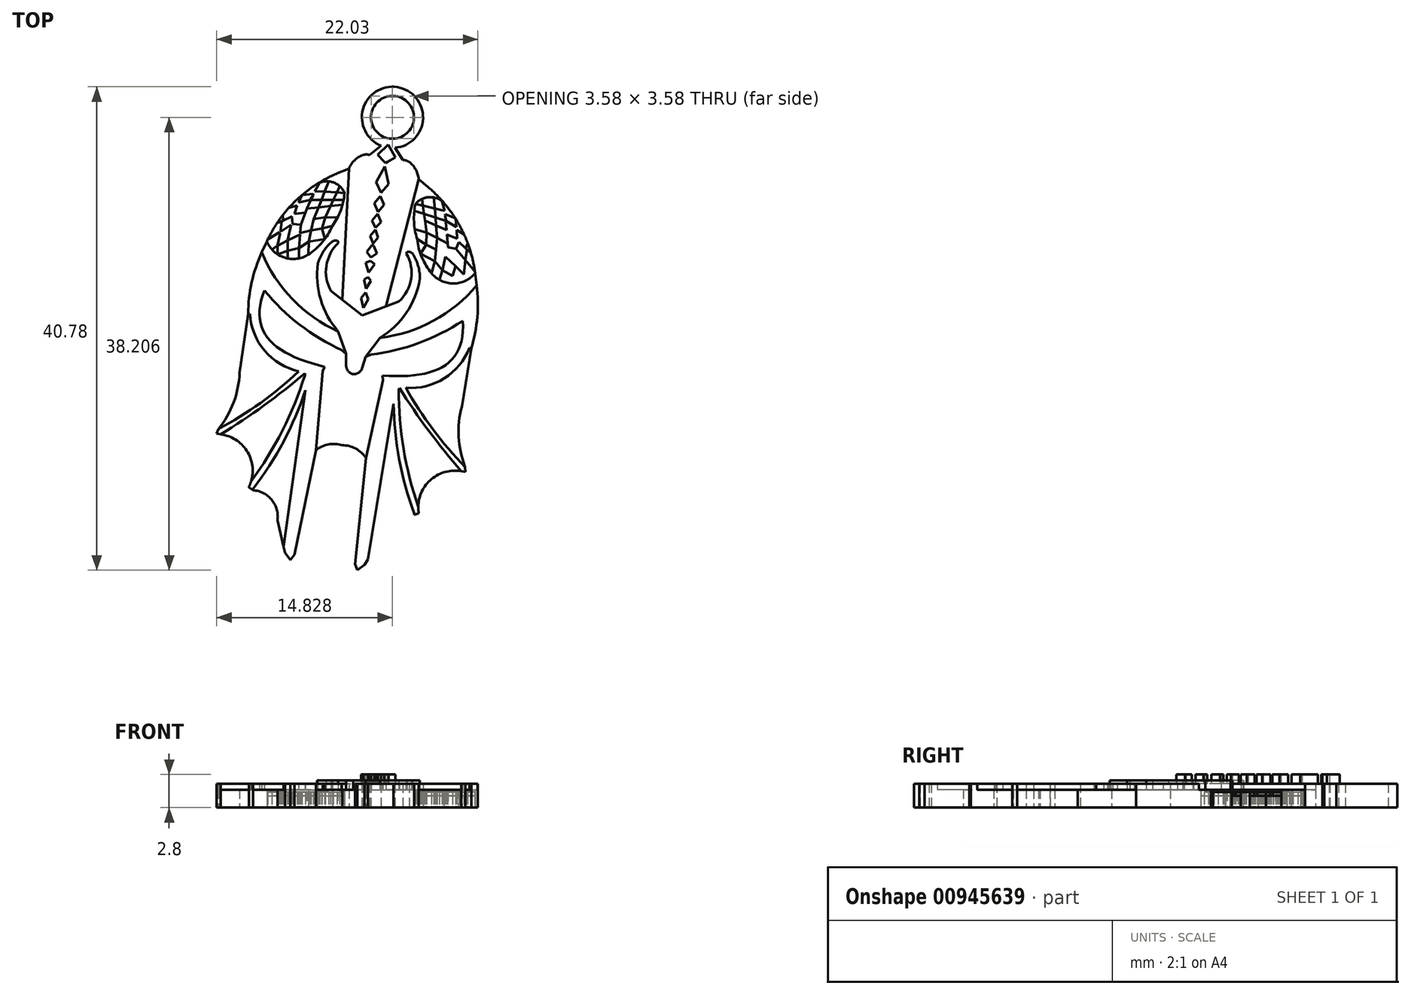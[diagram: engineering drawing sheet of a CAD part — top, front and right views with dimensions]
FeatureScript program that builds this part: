
annotation { "Feature Type Name" : "Feature", "Feature Type Description" : "" }
export const myFeature = defineFeature(function(context is Context, id is Id, definition is map)
    precondition{}
    {
        {
            var Q0;
            Q0=qCreatedBy(makeId("Top.planeOp"),FACE);
            var sketch = newSketch(context, id + "F0", { "sketchPlane" : qUnion([Q0])});
            skLineSegment(sketch, "E0", {"start": v(-25.56, -12.14) * mm, "end": v(-27.36, -20.95) * mm});
            skLineSegment(sketch, "E1", {"start": v(-25.56, -12.14) * mm, "end": v(-24.96, -5.46) * mm});
            skLineSegment(sketch, "E2", {"start": v(-24.96, -5.46) * mm, "end": v(-24.8, -5.09) * mm});
            skFitSpline(sketch, "E3", {"points": [v(-24.8, -5.09) * mm, v(-29.9, 1.35) * mm], "startDerivative": vector(-13.26, 3.2) * mm, "endDerivative": vector(4.1, 10.34) * mm});
            skLineSegment(sketch, "E4", {"start": v(-27.36, -20.95) * mm, "end": v(-27.7, -21.38) * mm});
            skLineSegment(sketch, "E5", {"start": v(-21.36, -21.48) * mm, "end": v(-21.23, -22.05) * mm});
            skArc(sketch, "E6", {"start": v(-29.9, 1.35) * mm, "mid": v(-26.93, -1.53) * mm, "end": v(-23.38, -3.66) * mm});
            skLineSegment(sketch, "E7", {"start": v(-19.37, 14.19) * mm, "end": v(-25.29, -24.47) * mm});
            skArc(sketch, "E8", {"start": v(-31.21, -15.24) * mm, "mid": v(-31.25, -12.4) * mm, "end": v(-33.58, -10.79) * mm});
            skArc(sketch, "E9", {"start": v(-28.8, -18.07) * mm, "mid": v(-29.26, -16.34) * mm, "end": v(-30.84, -15.5) * mm});
            skLineSegment(sketch, "E10", {"start": v(-28.8, -18.07) * mm, "end": v(-28.16, -20.77) * mm});
            skLineSegment(sketch, "E11", {"start": v(-28.16, -20.77) * mm, "end": v(-27.7, -21.38) * mm});
            skLineSegment(sketch, "E12", {"start": v(-31.21, -15.24) * mm, "end": v(-30.84, -15.5) * mm});
            skArc(sketch, "E13", {"start": v(-33.78, -10.35) * mm, "mid": v(-32.5, -8.1) * mm, "end": v(-31.98, -5.57) * mm});
            skLineSegment(sketch, "E14", {"start": v(-33.78, -10.35) * mm, "end": v(-33.92, -10.73) * mm});
            skLineSegment(sketch, "E15", {"start": v(-33.92, -10.73) * mm, "end": v(-33.58, -10.79) * mm});
            skLineSegment(sketch, "E16", {"start": v(-31.98, -5.57) * mm, "end": v(-31.26, -0.63) * mm});
            skArc(sketch, "E17", {"start": v(-30.12, 4.57) * mm, "mid": v(-30.97, 2.04) * mm, "end": v(-31.26, -0.63) * mm});
            skLineSegment(sketch, "E18", {"start": v(-30.12, 4.57) * mm, "end": v(-29.69, 5.5) * mm});
            skArc(sketch, "E19", {"start": v(-23.73, 11.24) * mm, "mid": v(-27.25, 8.93) * mm, "end": v(-29.69, 5.5) * mm});
            skLineSegment(sketch, "E20", {"start": v(-23.73, 11.24) * mm, "end": v(-22.77, 11.65) * mm});
            skArc(sketch, "E21", {"start": v(-21.57, 12.8) * mm, "mid": v(-22.29, 12.34) * mm, "end": v(-22.77, 11.65) * mm});
            skArc(sketch, "E22", {"start": v(-21.01, 12.8) * mm, "mid": v(-21.3, 12.83) * mm, "end": v(-21.57, 12.8) * mm});
            skLineSegment(sketch, "E23", {"start": v(-21.01, 12.8) * mm, "end": v(-19.98, 13.65) * mm});
            skLineSegment(sketch, "E24", {"start": v(-19.98, 13.65) * mm, "end": v(-19.37, 14.18) * mm});
            skArc(sketch, "E25", {"start": v(-23.34, -11.72) * mm, "mid": v(-24.5, -11.64) * mm, "end": v(-25.56, -12.14) * mm});
            skLineSegment(sketch, "E26", {"start": v(-23.38, -3.66) * mm, "end": v(-23, -4) * mm});
            skLineSegment(sketch, "E27", {"start": v(-23, -4) * mm, "end": v(-23, -4.97) * mm});
            skArc(sketch, "E28", {"start": v(-23, -4.97) * mm, "mid": v(-22.83, -5.44) * mm, "end": v(-22.42, -5.71) * mm});
            skArc(sketch, "E29", {"start": v(-31.12, -0.63) * mm, "mid": v(-29.87, -3.73) * mm, "end": v(-27, -5.47) * mm});
            skLineSegment(sketch, "E30", {"start": v(-31.12, -0.63) * mm, "end": v(-31.26, -0.63) * mm});
            skArc(sketch, "E31", {"start": v(-33.78, -10.35) * mm, "mid": v(-30.23, -8.13) * mm, "end": v(-27, -5.47) * mm});
            skArc(sketch, "E32", {"start": v(-33.58, -10.79) * mm, "mid": v(-29.93, -8.35) * mm, "end": v(-26.48, -5.64) * mm});
            skArc(sketch, "E33", {"start": v(-31.02, -14.75) * mm, "mid": v(-28.38, -10.47) * mm, "end": v(-26.48, -5.8) * mm});
            skLineSegment(sketch, "E34", {"start": v(-26.48, -5.8) * mm, "end": v(-26.48, -5.64) * mm});
            skArc(sketch, "E35", {"start": v(-30.84, -15.38) * mm, "mid": v(-28.29, -11.4) * mm, "end": v(-26.42, -7.06) * mm});
            skPoint(sketch, "E35.startSnap0", {"position": v(-31.03, -15.38) * mm});
            skLineSegment(sketch, "E36", {"start": v(-26.42, -7.06) * mm, "end": v(-28.28, -20.26) * mm});
            skArc(sketch, "E37", {"start": v(-30.12, 4.57) * mm, "mid": v(-27.53, 0.62) * mm, "end": v(-23.66, -2.1) * mm});
            skLineSegment(sketch, "E38", {"start": v(-23.66, -2.1) * mm, "end": v(-23, -4) * mm});
            skArc(sketch, "E39", {"start": v(-29.69, 5.5) * mm, "mid": v(-28.2, 4.12) * mm, "end": v(-26.19, 4.39) * mm});
            skArc(sketch, "E40", {"start": v(-26.19, 4.39) * mm, "mid": v(-25, 5.44) * mm, "end": v(-24.15, 6.8) * mm});
            skArc(sketch, "E41", {"start": v(-24.15, 6.8) * mm, "mid": v(-23.46, 8.12) * mm, "end": v(-23.14, 9.58) * mm});
            skArc(sketch, "E42", {"start": v(-23.14, 9.58) * mm, "mid": v(-24.22, 10.52) * mm, "end": v(-25.62, 10.24) * mm});
            skArc(sketch, "E43", {"start": v(-25.39, 3.66) * mm, "mid": v(-25.15, 0.59) * mm, "end": v(-23.66, -2.1) * mm});
            skArc(sketch, "E44", {"start": v(-24.15, 5.5) * mm, "mid": v(-24.9, 4.67) * mm, "end": v(-25.39, 3.66) * mm});
            skArc(sketch, "E45", {"start": v(-23.66, 5.5) * mm, "mid": v(-23.9, 5.57) * mm, "end": v(-24.15, 5.5) * mm});
            skLineSegment(sketch, "E46", {"start": v(-23.66, 5.5) * mm, "end": v(-23.66, 5.35) * mm});
            skArc(sketch, "E47", {"start": v(-23.66, 5.35) * mm, "mid": v(-24.67, 3.43) * mm, "end": v(-24.26, 1.3) * mm});
            skLineSegment(sketch, "E48", {"start": v(-24.26, 1.3) * mm, "end": v(-21.66, -0.76) * mm});
            skLineSegment(sketch, "E49", {"start": v(-22.77, 11.65) * mm, "end": v(-23.33, 0.57) * mm});
            skLineSegment(sketch, "E50", {"start": v(-29.62, 5.65) * mm, "end": v(-28.62, 6.27) * mm});
            skLineSegment(sketch, "E51", {"start": v(-28.54, 6.4) * mm, "end": v(-28.42, 7.15) * mm});
            skLineSegment(sketch, "E52", {"start": v(-28.42, 7.15) * mm, "end": v(-28.82, 7.06) * mm});
            skLineSegment(sketch, "E53", {"start": v(-28.82, 7.06) * mm, "end": v(-28.3, 7.26) * mm});
            skLineSegment(sketch, "E54", {"start": v(-28.3, 7.26) * mm, "end": v(-28.34, 7.72) * mm});
            skLineSegment(sketch, "E55", {"start": v(-28.3, 7.26) * mm, "end": v(-28.42, 7.15) * mm});
            skLineSegment(sketch, "E56", {"start": v(-27.6, 7.6) * mm, "end": v(-28.3, 7.26) * mm});
            skLineSegment(sketch, "E57", {"start": v(-27.6, 7.6) * mm, "end": v(-27.53, 6.98) * mm});
            skLineSegment(sketch, "E58", {"start": v(-27.53, 6.98) * mm, "end": v(-28.5, 6.34) * mm});
            skLineSegment(sketch, "E59", {"start": v(-27.82, 8.34) * mm, "end": v(-27.12, 8.53) * mm});
            skLineSegment(sketch, "E60", {"start": v(-27.12, 8.53) * mm, "end": v(-27.35, 7.83) * mm});
            skLineSegment(sketch, "E61", {"start": v(-27.35, 7.83) * mm, "end": v(-27.6, 7.6) * mm});
            skLineSegment(sketch, "E62", {"start": v(-27.12, 8.53) * mm, "end": v(-26.72, 9.42) * mm});
            skLineSegment(sketch, "E63", {"start": v(-26.72, 9.42) * mm, "end": v(-25.79, 9.51) * mm});
            skLineSegment(sketch, "E64", {"start": v(-25.79, 9.51) * mm, "end": v(-25.22, 10.46) * mm});
            skLineSegment(sketch, "E65", {"start": v(-25.79, 9.4) * mm, "end": v(-26.04, 8.99) * mm});
            skLineSegment(sketch, "E66", {"start": v(-26.04, 8.99) * mm, "end": v(-27.02, 8.76) * mm});
            skLineSegment(sketch, "E67", {"start": v(-26.04, 8.9) * mm, "end": v(-26.84, 6.92) * mm});
            skLineSegment(sketch, "E68", {"start": v(-26.84, 6.92) * mm, "end": v(-27.53, 6.98) * mm});
            skLineSegment(sketch, "E69", {"start": v(-26.44, 7.9) * mm, "end": v(-27.35, 7.83) * mm});
            skLineSegment(sketch, "E70", {"start": v(-25.79, 9.4) * mm, "end": v(-25.79, 9.51) * mm});
            skLineSegment(sketch, "E71", {"start": v(-26.04, 8.9) * mm, "end": v(-26.04, 8.99) * mm});
            skLineSegment(sketch, "E72", {"start": v(-28.58, 6.2) * mm, "end": v(-28.78, 5.16) * mm});
            skLineSegment(sketch, "E73", {"start": v(-28.81, 5.11) * mm, "end": v(-29.26, 4.82) * mm});
            skLineSegment(sketch, "E74", {"start": v(-28.8, 5.1) * mm, "end": v(-28.8, 4.4) * mm});
            skLineSegment(sketch, "E75", {"start": v(-28.8, 4.4) * mm, "end": v(-27.93, 4.72) * mm});
            skLineSegment(sketch, "E76", {"start": v(-27.93, 4.72) * mm, "end": v(-27.93, 5.53) * mm});
            skLineSegment(sketch, "E77", {"start": v(-27.98, 5.57) * mm, "end": v(-28.78, 5.13) * mm});
            skLineSegment(sketch, "E78", {"start": v(-27.92, 5.64) * mm, "end": v(-27.64, 6.9) * mm});
            skLineSegment(sketch, "E79", {"start": v(-27.64, 6.9) * mm, "end": v(-27.92, 5.64) * mm});
            skLineSegment(sketch, "E80", {"start": v(-27.9, 5.6) * mm, "end": v(-26.88, 6.07) * mm});
            skLineSegment(sketch, "E81", {"start": v(-26.88, 6.07) * mm, "end": v(-26.84, 6.92) * mm});
            skLineSegment(sketch, "E82", {"start": v(-26.88, 6.07) * mm, "end": v(-26.98, 4.92) * mm});
            skLineSegment(sketch, "E83", {"start": v(-26.98, 4.92) * mm, "end": v(-27.93, 4.72) * mm});
            skLineSegment(sketch, "E84", {"start": v(-26.98, 4.92) * mm, "end": v(-26.98, 4.06) * mm});
            skLineSegment(sketch, "E85", {"start": v(-26.98, 4.06) * mm, "end": v(-26.98, 4.92) * mm});
            skLineSegment(sketch, "E86", {"start": v(-26.98, 4.92) * mm, "end": v(-26.15, 5.47) * mm});
            skLineSegment(sketch, "E87", {"start": v(-26.15, 5.47) * mm, "end": v(-26.19, 4.39) * mm});
            skLineSegment(sketch, "E88", {"start": v(-26.15, 5.47) * mm, "end": v(-24.8, 5.7) * mm});
            skLineSegment(sketch, "E89", {"start": v(-24.8, 5.7) * mm, "end": v(-25.04, 6.57) * mm});
            skLineSegment(sketch, "E90", {"start": v(-25.04, 6.57) * mm, "end": v(-25.95, 6.41) * mm});
            skLineSegment(sketch, "E91", {"start": v(-25.95, 6.41) * mm, "end": v(-26.88, 6.2) * mm});
            skLineSegment(sketch, "E92", {"start": v(-26.88, 6.2) * mm, "end": v(-25.95, 6.41) * mm});
            skLineSegment(sketch, "E93", {"start": v(-25.95, 6.41) * mm, "end": v(-26.15, 5.47) * mm});
            skLineSegment(sketch, "E94", {"start": v(-25.04, 6.57) * mm, "end": v(-24.15, 6.8) * mm});
            skLineSegment(sketch, "E95", {"start": v(-25.04, 6.57) * mm, "end": v(-24.75, 7.55) * mm});
            skLineSegment(sketch, "E96", {"start": v(-24.75, 7.55) * mm, "end": v(-23.72, 7.51) * mm});
            skLineSegment(sketch, "E97", {"start": v(-23.72, 7.51) * mm, "end": v(-24.75, 7.55) * mm});
            skLineSegment(sketch, "E98", {"start": v(-24.75, 7.55) * mm, "end": v(-26.72, 7.2) * mm});
            skLineSegment(sketch, "E99", {"start": v(-26.72, 7.2) * mm, "end": v(-25.74, 7.38) * mm});
            skLineSegment(sketch, "E100", {"start": v(-25.74, 7.38) * mm, "end": v(-25.95, 6.41) * mm});
            skLineSegment(sketch, "E101", {"start": v(-25.74, 7.38) * mm, "end": v(-24.45, 10.56) * mm});
            skLineSegment(sketch, "E102", {"start": v(-24.75, 7.55) * mm, "end": v(-23.53, 10.14) * mm});
            skLineSegment(sketch, "E103", {"start": v(-26.3, 8.25) * mm, "end": v(-23.3, 8.6) * mm});
            skLineSegment(sketch, "E104", {"start": v(-25.65, 9.74) * mm, "end": v(-23.14, 9.58) * mm});
            skLineSegment(sketch, "E105", {"start": v(-26.04, 8.99) * mm, "end": v(-23.22, 8.99) * mm});
            skLineSegment(sketch, "E106", {"start": v(-20.95, 3.86) * mm, "end": v(-21.37, 3.69) * mm});
            skLineSegment(sketch, "E107", {"start": v(-21.37, 3.69) * mm, "end": v(-21.1, 2.86) * mm});
            skLineSegment(sketch, "E108", {"start": v(-21.16, 2.5) * mm, "end": v(-21.5, 2.27) * mm});
            skLineSegment(sketch, "E109", {"start": v(-21.5, 2.27) * mm, "end": v(-21.3, 1.5) * mm});
            skLineSegment(sketch, "E110", {"start": v(-21.36, 1.2) * mm, "end": v(-21.74, 0.71) * mm});
            skLineSegment(sketch, "E111", {"start": v(-21.74, 0.71) * mm, "end": v(-21.56, -0.12) * mm});
            skLineSegment(sketch, "E112", {"start": v(-19.45, 13.66) * mm, "end": v(-20.34, 12.81) * mm});
            skLineSegment(sketch, "E113", {"start": v(-20.34, 12.81) * mm, "end": v(-19.8, 12.25) * mm});
            skLineSegment(sketch, "E114", {"start": v(-19.73, 11.84) * mm, "end": v(-20.48, 10.49) * mm});
            skLineSegment(sketch, "E115", {"start": v(-20.48, 10.49) * mm, "end": v(-20.07, 9.6) * mm});
            skLineSegment(sketch, "E116", {"start": v(-19.8, 12.25) * mm, "end": v(-19.68, 12.12) * mm});
            skLineSegment(sketch, "E117", {"start": v(-20.8, 5.17) * mm, "end": v(-21.27, 4.62) * mm});
            skLineSegment(sketch, "E118", {"start": v(-21.27, 4.62) * mm, "end": v(-20.9, 4.14) * mm});
            skLineSegment(sketch, "E119", {"start": v(-20.55, 6.5) * mm, "end": v(-20.98, 5.94) * mm});
            skLineSegment(sketch, "E120", {"start": v(-20.98, 5.94) * mm, "end": v(-20.72, 5.32) * mm});
            skLineSegment(sketch, "E121", {"start": v(-20.34, 7.83) * mm, "end": v(-20.82, 7.24) * mm});
            skLineSegment(sketch, "E122", {"start": v(-20.82, 7.24) * mm, "end": v(-20.52, 6.65) * mm});
            skLineSegment(sketch, "E123", {"start": v(-20.11, 9.32) * mm, "end": v(-20.64, 8.7) * mm});
            skLineSegment(sketch, "E124", {"start": v(-20.64, 8.7) * mm, "end": v(-20.32, 8) * mm});
            skLineSegment(sketch, "E125.MirrorCS", {"start": v(-13.49, 5.43) * mm, "end": v(-12.92, 4.9) * mm});
            skLineSegment(sketch, "E126.MirrorCS", {"start": v(-13.77, 3.42) * mm, "end": v(-13.65, 4.76) * mm});
            skLineSegment(sketch, "E127.MirrorCS", {"start": v(-12.92, 4.9) * mm, "end": v(-12.74, 5.33) * mm});
            skLineSegment(sketch, "E128.MirrorCS", {"start": v(-14.6, 4.32) * mm, "end": v(-15.4, 4.8) * mm});
            skLineSegment(sketch, "E129.MirrorCS", {"start": v(-14.59, 7.14) * mm, "end": v(-14.56, 7.23) * mm});
            skLineSegment(sketch, "E130.MirrorCS", {"start": v(-14.67, 7.7) * mm, "end": v(-14.64, 7.8) * mm});
            skLineSegment(sketch, "E131.MirrorCS", {"start": v(-12.48, 4.56) * mm, "end": v(-12.92, 4.9) * mm});
            skLineSegment(sketch, "E132.MirrorCS", {"start": v(-13.65, 4.76) * mm, "end": v(-13.77, 3.42) * mm});
            skLineSegment(sketch, "E133.MirrorCS", {"start": v(-13.49, 5.43) * mm, "end": v(-13.73, 4.87) * mm});
            skLineSegment(sketch, "E134.MirrorCS", {"start": v(-14.63, 4.19) * mm, "end": v(-14.42, 5.01) * mm});
            skLineSegment(sketch, "E135.MirrorCS", {"start": v(-13.66, 6.47) * mm, "end": v(-13.65, 5.73) * mm});
            skLineSegment(sketch, "E136.MirrorCS", {"start": v(-15.4, 4.8) * mm, "end": v(-14.6, 4.32) * mm});
            skLineSegment(sketch, "E137.MirrorCS", {"start": v(-14.44, 5.32) * mm, "end": v(-15.33, 5.78) * mm});
            skLineSegment(sketch, "E138.MirrorCS", {"start": v(-13.66, 6.47) * mm, "end": v(-13.78, 7.43) * mm});
            skLineSegment(sketch, "E139.MirrorCS", {"start": v(-13.73, 4.87) * mm, "end": v(-12.95, 3.91) * mm});
            skLineSegment(sketch, "E140.MirrorCS", {"start": v(-14.5, 6.08) * mm, "end": v(-13.65, 5.73) * mm});
            skLineSegment(sketch, "E141.MirrorCS", {"start": v(-12.14, 2.97) * mm, "end": v(-12.95, 3.91) * mm});
            skLineSegment(sketch, "E142.MirrorCS", {"start": v(-14.56, 7.23) * mm, "end": v(-13.69, 6.72) * mm});
            skLineSegment(sketch, "E143.MirrorCS", {"start": v(-13.05, 6.08) * mm, "end": v(-13.66, 6.47) * mm});
            skLineSegment(sketch, "E144.MirrorCS", {"start": v(-14.67, 7.7) * mm, "end": v(-14.56, 7.23) * mm});
            skLineSegment(sketch, "E145.MirrorCS", {"start": v(-13.78, 7.43) * mm, "end": v(-14.64, 7.8) * mm});
            skLineSegment(sketch, "E146.MirrorCS", {"start": v(-13.65, 5.73) * mm, "end": v(-13.49, 5.43) * mm});
            skLineSegment(sketch, "E147.MirrorCS", {"start": v(-14.03, 2.59) * mm, "end": v(-13.77, 3.42) * mm});
            skLineSegment(sketch, "E148.MirrorCS", {"start": v(-15.33, 5.78) * mm, "end": v(-15.4, 4.8) * mm});
            skLineSegment(sketch, "E149.MirrorCS", {"start": v(-15.33, 5.78) * mm, "end": v(-15.6, 9.2) * mm});
            skLineSegment(sketch, "E150.MirrorCS", {"start": v(-12.95, 3.91) * mm, "end": v(-12.83, 4.76) * mm});
            skLineSegment(sketch, "E151.MirrorCS", {"start": v(-16.23, 5.22) * mm, "end": v(-15.4, 4.8) * mm});
            skLineSegment(sketch, "E152.MirrorCS", {"start": v(-13.77, 3.42) * mm, "end": v(-14.63, 4.19) * mm});
            skLineSegment(sketch, "E153.MirrorCS", {"start": v(-14.59, 7.14) * mm, "end": v(-14.42, 5.01) * mm});
            skLineSegment(sketch, "E154.MirrorCS", {"start": v(-16.23, 5.22) * mm, "end": v(-16.21, 6.24) * mm});
            skLineSegment(sketch, "E155.MirrorCS", {"start": v(-14.64, 7.8) * mm, "end": v(-14.9, 8.88) * mm});
            skLineSegment(sketch, "E156.MirrorCS", {"start": v(-14.42, 5.01) * mm, "end": v(-13.73, 4.87) * mm});
            skLineSegment(sketch, "E157.MirrorCS", {"start": v(-15.5, 3.84) * mm, "end": v(-16.73, 4.46) * mm});
            skLineSegment(sketch, "E158.MirrorCS", {"start": v(-12.92, 4.9) * mm, "end": v(-12.83, 4.76) * mm});
            skLineSegment(sketch, "E159.MirrorCS", {"start": v(-12.83, 4.76) * mm, "end": v(-12.48, 4.56) * mm});
            skLineSegment(sketch, "E160.MirrorCS", {"start": v(-17.87, 4.62) * mm, "end": v(-17.91, 4.47) * mm});
            skLineSegment(sketch, "E161.MirrorCS", {"start": v(-14.88, 3.07) * mm, "end": v(-15.5, 3.84) * mm});
            skLineSegment(sketch, "E162.MirrorCS", {"start": v(-15.14, 2.25) * mm, "end": v(-14.88, 3.07) * mm});
            skLineSegment(sketch, "E163.MirrorCS", {"start": v(-15.4, 4.8) * mm, "end": v(-15.5, 3.84) * mm});
            skLineSegment(sketch, "E164.MirrorCS", {"start": v(-13.09, 2.72) * mm, "end": v(-13.3, 2.03) * mm});
            skLineSegment(sketch, "E165.MirrorCS", {"start": v(-16.21, 6.24) * mm, "end": v(-14.44, 5.32) * mm});
            skLineSegment(sketch, "E166.MirrorCS", {"start": v(-14.63, 4.19) * mm, "end": v(-14.88, 3.07) * mm});
            skLineSegment(sketch, "E167.MirrorCS", {"start": v(-12.95, 3.91) * mm, "end": v(-13.09, 2.72) * mm});
            skLineSegment(sketch, "E168.MirrorCS", {"start": v(-17.2, 6.52) * mm, "end": v(-16.21, 6.24) * mm});
            skLineSegment(sketch, "E169.MirrorCS", {"start": v(-16.73, 4.46) * mm, "end": v(-16.23, 5.22) * mm});
            skLineSegment(sketch, "E170.MirrorCS", {"start": v(-14.88, 3.07) * mm, "end": v(-14.03, 2.59) * mm});
            skArc(sketch, "E171.MirrorCS", {"start": v(-15.8, 2.8) * mm, "mid": v(-16.61, 4.16) * mm, "end": v(-17.01, 5.7) * mm});
            skLineSegment(sketch, "E172.MirrorCS", {"start": v(-16.23, 5.22) * mm, "end": v(-17.01, 5.7) * mm});
            skLineSegment(sketch, "E173.MirrorCS", {"start": v(-13.3, 2.03) * mm, "end": v(-14.03, 2.59) * mm});
            skArc(sketch, "E174.MirrorCS", {"start": v(-17.87, 4.62) * mm, "mid": v(-17.62, 4.6) * mm, "end": v(-17.4, 4.47) * mm});
            skArc(sketch, "E175.MirrorCS", {"start": v(-17.4, 4.47) * mm, "mid": v(-16.93, 3.45) * mm, "end": v(-16.78, 2.34) * mm});
            skLineSegment(sketch, "E176.MirrorCS", {"start": v(-13.77, 3.42) * mm, "end": v(-13.09, 2.72) * mm});
            skLineSegment(sketch, "E177.MirrorCS", {"start": v(-16.21, 6.24) * mm, "end": v(-17.2, 6.52) * mm});
            skLineSegment(sketch, "E178.MirrorCS", {"start": v(-14.88, 3.07) * mm, "end": v(-15.14, 2.25) * mm});
            skLineSegment(sketch, "E179.MirrorCS", {"start": v(-15.5, 3.84) * mm, "end": v(-15.8, 2.8) * mm});
            skLineSegment(sketch, "E180.MirrorCS", {"start": v(-13.09, 2.72) * mm, "end": v(-12.73, 2.28) * mm});
            skLineSegment(sketch, "E181.MirrorCS", {"start": v(-14.7, 8.07) * mm, "end": v(-17.15, 8.66) * mm});
            skArc(sketch, "E182.MirrorCS", {"start": v(-12.12, 2.81) * mm, "mid": v(-13.95, 1.94) * mm, "end": v(-15.8, 2.8) * mm});
            skLineSegment(sketch, "E183.MirrorCS", {"start": v(-19.9, -6.23) * mm, "end": v(-19.94, -5.83) * mm});
            skLineSegment(sketch, "E184.MirrorCS", {"start": v(-20.88, -4.05) * mm, "end": v(-21.35, -4.25) * mm});
            skArc(sketch, "E185.MirrorCS", {"start": v(-17.01, 5.7) * mm, "mid": v(-17.28, 7.17) * mm, "end": v(-17.15, 8.66) * mm});
            skArc(sketch, "E186.MirrorCS", {"start": v(-17.15, 8.66) * mm, "mid": v(-15.84, 9.23) * mm, "end": v(-14.58, 8.55) * mm});
            skLineSegment(sketch, "E187.MirrorCS", {"start": v(-14.56, 7.23) * mm, "end": v(-17.25, 8.07) * mm});
            skLineSegment(sketch, "E188.MirrorCS", {"start": v(-19.53, 12.2) * mm, "end": v(-19.68, 12.12) * mm});
            skLineSegment(sketch, "E189.MirrorCS", {"start": v(-16.21, 6.24) * mm, "end": v(-16.6, 9.08) * mm});
            skLineSegment(sketch, "E190.MirrorCS", {"start": v(-11.99, 1.8) * mm, "end": v(-12.12, 2.81) * mm});
            skArc(sketch, "E191.MirrorCS", {"start": v(-18.2, 12.37) * mm, "mid": v(-17.93, 12.31) * mm, "end": v(-17.68, 12.2) * mm});
            skLineSegment(sketch, "E192.MirrorCS", {"start": v(-20.15, -2.64) * mm, "end": v(-21.35, -4.25) * mm});
            skLineSegment(sketch, "E193.MirrorCS", {"start": v(-21.35, -4.25) * mm, "end": v(-21.64, -5.18) * mm});
            skLineSegment(sketch, "E194.MirrorCS", {"start": v(-16.08, 10.07) * mm, "end": v(-16.88, 10.75) * mm});
            skLineSegment(sketch, "E195.MirrorCS", {"start": v(-14.53, 6.45) * mm, "end": v(-17.28, 7.67) * mm});
            skArc(sketch, "E196.MirrorCS", {"start": v(-16.08, 10.07) * mm, "mid": v(-13.42, 6.81) * mm, "end": v(-12.12, 2.81) * mm});
            skLineSegment(sketch, "E197.MirrorCS", {"start": v(-20.55, 6.5) * mm, "end": v(-20.3, 5.84) * mm});
            skLineSegment(sketch, "E198.MirrorCS", {"start": v(-20.06, 7.12) * mm, "end": v(-20.52, 6.65) * mm});
            skLineSegment(sketch, "E199.MirrorCS", {"start": v(-20.69, 5.15) * mm, "end": v(-20.42, 4.49) * mm});
            skLineSegment(sketch, "E200.MirrorCS", {"start": v(-20.11, 9.32) * mm, "end": v(-19.8, 8.57) * mm});
            skLineSegment(sketch, "E201.MirrorCS", {"start": v(-20.95, 3.86) * mm, "end": v(-20.6, 3.57) * mm});
            skLineSegment(sketch, "E202.MirrorCS", {"start": v(-21.36, 1.2) * mm, "end": v(-21.14, 0.62) * mm});
            skLineSegment(sketch, "E203.MirrorCS", {"start": v(-18.2, 12.37) * mm, "end": v(-18.94, 13.49) * mm});
            skLineSegment(sketch, "E204.MirrorCS", {"start": v(-19.73, 11.84) * mm, "end": v(-19.4, 10.32) * mm});
            skLineSegment(sketch, "E205.MirrorCS", {"start": v(-18.56, -7.02) * mm, "end": v(-18.51, -6.86) * mm});
            skLineSegment(sketch, "E206.MirrorCS", {"start": v(-16.88, -17.44) * mm, "end": v(-17.3, -17.58) * mm});
            skLineSegment(sketch, "E207.MirrorCS", {"start": v(-20.9, 2.17) * mm, "end": v(-21.3, 1.5) * mm});
            skLineSegment(sketch, "E208.MirrorCS", {"start": v(-20.42, 4.49) * mm, "end": v(-20.9, 4.14) * mm});
            skLineSegment(sketch, "E209.MirrorCS", {"start": v(-19.8, 8.57) * mm, "end": v(-20.32, 8) * mm});
            skLineSegment(sketch, "E210.MirrorCS", {"start": v(-18.85, 12.58) * mm, "end": v(-19.53, 12.2) * mm});
            skLineSegment(sketch, "E211.MirrorCS", {"start": v(-21.16, 2.5) * mm, "end": v(-20.9, 2.17) * mm});
            skArc(sketch, "E212.MirrorCS", {"start": v(-17.68, 12.2) * mm, "mid": v(-17.13, 11.55) * mm, "end": v(-16.88, 10.75) * mm});
            skLineSegment(sketch, "E213.MirrorCS", {"start": v(-19.45, 13.66) * mm, "end": v(-18.85, 12.58) * mm});
            skLineSegment(sketch, "E214.MirrorCS", {"start": v(-19.4, 10.32) * mm, "end": v(-20.07, 9.6) * mm});
            skLineSegment(sketch, "E215.MirrorCS", {"start": v(-20.6, 3.57) * mm, "end": v(-21.1, 2.86) * mm});
            skLineSegment(sketch, "E216.MirrorCS", {"start": v(-12.59, -3.47) * mm, "end": v(-12.45, -3.5) * mm});
            skLineSegment(sketch, "E217.MirrorCS", {"start": v(-20.3, 5.84) * mm, "end": v(-20.72, 5.32) * mm});
            skLineSegment(sketch, "E218.MirrorCS", {"start": v(-20.34, 7.83) * mm, "end": v(-20.06, 7.12) * mm});
            skLineSegment(sketch, "E219.MirrorCS", {"start": v(-22.26, -21.73) * mm, "end": v(-22.07, -22.24) * mm});
            skArc(sketch, "E220.MirrorCS", {"start": v(-11.99, 1.8) * mm, "mid": v(-11.93, -0.88) * mm, "end": v(-12.45, -3.5) * mm});
            skLineSegment(sketch, "E221.MirrorCS", {"start": v(-12.96, -13.54) * mm, "end": v(-12.94, -13.95) * mm});
            skLineSegment(sketch, "E222.MirrorCS", {"start": v(-21.45, -21.8) * mm, "end": v(-22.07, -22.24) * mm});
            skLineSegment(sketch, "E223.MirrorCS", {"start": v(-12.94, -13.95) * mm, "end": v(-13.28, -13.9) * mm});
            skLineSegment(sketch, "E224.MirrorCS", {"start": v(-16.88, 10.75) * mm, "end": v(-19.66, 0) * mm});
            skLineSegment(sketch, "E225.MirrorCS", {"start": v(-21.14, 0.62) * mm, "end": v(-21.56, -0.12) * mm});
            skLineSegment(sketch, "E226.MirrorCS", {"start": v(-18.55, 0.42) * mm, "end": v(-21.66, -0.76) * mm});
            skArc(sketch, "E227.MirrorCS", {"start": v(-21.64, -5.18) * mm, "mid": v(-21.93, -5.58) * mm, "end": v(-22.42, -5.71) * mm});
            skArc(sketch, "E228.MirrorCS", {"start": v(-20.03, -19.41) * mm, "mid": v(-19.07, -17.9) * mm, "end": v(-17.3, -17.58) * mm});
            skLineSegment(sketch, "E229.MirrorCS", {"start": v(-28.14, -20.44) * mm, "end": v(-28.44, -20.95) * mm});
            skArc(sketch, "E230.MirrorCS", {"start": v(-16.78, 2.34) * mm, "mid": v(-17.92, -0.52) * mm, "end": v(-20.15, -2.64) * mm});
            skLineSegment(sketch, "E231.MirrorCS", {"start": v(-18.94, 13.49) * mm, "end": v(-19.37, 14.18) * mm});
            skArc(sketch, "E232.MirrorCS", {"start": v(-17.91, 4.47) * mm, "mid": v(-17.52, 2.34) * mm, "end": v(-18.55, 0.42) * mm});
            skLineSegment(sketch, "E233.MirrorCS", {"start": v(-20.03, -19.41) * mm, "end": v(-21.45, -21.8) * mm});
            skLineSegment(sketch, "E234.MirrorCS", {"start": v(-13.24, -8.44) * mm, "end": v(-12.45, -3.5) * mm});
            skArc(sketch, "E235.MirrorCS", {"start": v(-11.99, 1.8) * mm, "mid": v(-15.64, -1.2) * mm, "end": v(-20.15, -2.64) * mm});
            skArc(sketch, "E236.MirrorCS", {"start": v(-12.59, -3.47) * mm, "mid": v(-14.71, -6.06) * mm, "end": v(-17.97, -6.85) * mm});
            skFitSpline(sketch, "E237.MirrorCS", {"points": [v(-19.94, -5.83) * mm, v(-13.16, -1.21) * mm], "startDerivative": vector(13.61, -0.92) * mm, "endDerivative": vector(-0.83, 11.1) * mm});
            skArc(sketch, "E238.MirrorCS", {"start": v(-13.16, -1.21) * mm, "mid": v(-16.86, -3.08) * mm, "end": v(-20.88, -4.05) * mm});
            skArc(sketch, "E239.MirrorCS", {"start": v(-23.34, -11.72) * mm, "mid": v(-22.2, -11.99) * mm, "end": v(-21.33, -12.78) * mm});
            skLineSegment(sketch, "E240.MirrorCS", {"start": v(-19, -8.2) * mm, "end": v(-21.18, -21.35) * mm});
            skArc(sketch, "E241.MirrorCS", {"start": v(-16.88, -17.44) * mm, "mid": v(-16, -14.74) * mm, "end": v(-13.28, -13.9) * mm});
            skArc(sketch, "E242.MirrorCS", {"start": v(-12.96, -13.54) * mm, "mid": v(-15.69, -10.36) * mm, "end": v(-17.97, -6.85) * mm});
            skLineSegment(sketch, "E243.MirrorCS", {"start": v(-21.33, -12.78) * mm, "end": v(-19.9, -6.23) * mm});
            skArc(sketch, "E244.MirrorCS", {"start": v(-16.91, -16.9) * mm, "mid": v(-18.15, -12.04) * mm, "end": v(-18.56, -7.02) * mm});
            skArc(sketch, "E245.MirrorCS", {"start": v(-17.27, -17.46) * mm, "mid": v(-18.52, -12.9) * mm, "end": v(-19, -8.2) * mm});
            skLineSegment(sketch, "E246.MirrorCS", {"start": v(-21.33, -12.78) * mm, "end": v(-22.26, -21.73) * mm});
            skArc(sketch, "E247.MirrorCS", {"start": v(-13.28, -13.9) * mm, "mid": v(-16.03, -10.48) * mm, "end": v(-18.51, -6.86) * mm});
            skArc(sketch, "E248.MirrorCS", {"start": v(-12.96, -13.54) * mm, "mid": v(-13.51, -11.01) * mm, "end": v(-13.24, -8.44) * mm});
            skPoint(sketch, "E249.MirrorP", {"position": v(-17.1, -17.51) * mm});
            skCircle(sketch, "E250", {"center": v(-19.1, 15.97) * mm, "radius": 1.81 * mm});
            skCircle(sketch, "E251", {"center": v(-19.1, 15.97) * mm, "radius": 2.58 * mm});
            skLineSegment(sketch, "E252", {"start": v(-30.84, -15.38) * mm, "end": v(-30.89, -15.48) * mm});
            skLineSegment(sketch, "E253", {"start": v(-17.27, -17.46) * mm, "end": v(-17.25, -17.56) * mm});
            skLineSegment(sketch, "E254", {"start": v(-20.8, 5.17) * mm, "end": v(-20.74, 5.2) * mm});
            skLineSegment(sketch, "E255", {"start": v(-20.74, 5.2) * mm, "end": v(-20.7, 5.15) * mm});
            skLineSegment(sketch, "E256", {"start": v(-20.7, 5.15) * mm, "end": v(-20.69, 5.15) * mm});
            skLineSegment(sketch, "E257", {"start": v(-19.37, 14.18) * mm, "end": v(-19.37, 14.18) * mm});
            skLineSegment(sketch, "E258", {"start": v(-27.98, 5.57) * mm, "end": v(-27.93, 5.53) * mm});
            skLineSegment(sketch, "E259", {"start": v(-27.92, 5.64) * mm, "end": v(-27.9, 5.6) * mm});
            skLineSegment(sketch, "E260", {"start": v(-27.9, 5.6) * mm, "end": v(-27.9, 5.6) * mm});
            skLineSegment(sketch, "E261", {"start": v(-28.62, 6.27) * mm, "end": v(-28.58, 6.2) * mm});
            skLineSegment(sketch, "E262", {"start": v(-28.54, 6.4) * mm, "end": v(-28.5, 6.34) * mm});
            skPoint(sketch, "E263.orphan", {"position": v(-28.56, 6.3) * mm});
            skPoint(sketch, "E264.orphan", {"position": v(-27.93, 5.6) * mm});
            skLineSegment(sketch, "E265", {"start": v(-28.78, 5.13) * mm, "end": v(-28.8, 5.1) * mm});
            skLineSegment(sketch, "E266", {"start": v(-28.78, 5.16) * mm, "end": v(-28.81, 5.11) * mm});
            skPoint(sketch, "E267.orphan", {"position": v(-28.8, 5.13) * mm});
            skLineSegment(sketch, "E268", {"start": v(-27.93, 4.72) * mm, "end": v(-27.93, 4.06) * mm});
            skSolve(sketch);
        }
        {
            var Q0;
            Q0=makeQuery(id+"F0.imprint","IMPRINT",FACE,{"disambiguationData":[TD([[makeQuery(id+"F0.imprint","IMPRINT",EDGE,{"derivedFrom":sQuery(id+"F0.wireOp",EDGE,"E183.MirrorCS")}),1.0]])]});
            var Q1;
            Q1=makeQuery(id+"F0.imprint","IMPRINT",FACE,{"disambiguationData":[TD([[makeQuery(id+"F0.imprint","IMPRINT",EDGE,{"derivedFrom":sQuery(id+"F0.wireOp",EDGE,"E1")}),-1.0]])]});
            var Q2;
            Q2=makeQuery(id+"F0.imprint","IMPRINT",FACE,{"disambiguationData":[TD([[makeQuery(id+"F0.imprint","IMPRINT",EDGE,{"derivedFrom":sQuery(id+"F0.wireOp",EDGE,"E160.MirrorCS")}),-1.0]])]});
            var Q3;
            {var subQ17=sQuery(id+"F0.wireOp",EDGE,"E18");Q3=makeQuery(id+"F0.imprint","IMPRINT",FACE,{"disambiguationData":[TD([[makeQuery(id+"F0.imprint","IMPRINT",EDGE,{"derivedFrom":subQ17}),-1.0]])]});}
            extrude(context, id + "F1", {"entities" : qUnion([Q0, Q1, Q2, Q3]), "depth" : 1.5 * mm, "offsetDistance" : 25 * mm});
        }
        {
            var Q0;
            {var subQ2=sQuery(id+"F0.wireOp",EDGE,"E228.MirrorCS");Q0=makeQuery(id+"F0.imprint","IMPRINT",FACE,{"disambiguationData":[TD([[makeQuery(id+"F0.imprint","IMPRINT",EDGE,{"derivedFrom":subQ2}),1.0]])]});}
            var Q1;
            Q1=makeQuery(id+"F0.imprint","IMPRINT",FACE,{"disambiguationData":[TD([[makeQuery(id+"F0.imprint","IMPRINT",EDGE,{"derivedFrom":sQuery(id+"F0.wireOp",EDGE,"E205.MirrorCS")}),-1.0]])]});
            var Q2;
            Q2=makeQuery(id+"F0.imprint","IMPRINT",FACE,{"disambiguationData":[TD([[makeQuery(id+"F0.imprint","IMPRINT",EDGE,{"derivedFrom":sQuery(id+"F0.wireOp",EDGE,"E216.MirrorCS")}),-1.0]])]});
            var Q3;
            {var subQ1=sQuery(id+"F0.wireOp",EDGE,"E9");Q3=makeQuery(id+"F0.imprint","IMPRINT",FACE,{"disambiguationData":[TD([[makeQuery(id+"F0.imprint","IMPRINT",EDGE,{"derivedFrom":subQ1}),-1.0]])]});}
            var Q4;
            {var subQ0=sQuery(id+"F0.wireOp",EDGE,"E32");Q4=makeQuery(id+"F0.imprint","IMPRINT",FACE,{"disambiguationData":[TD([[makeQuery(id+"F0.imprint","IMPRINT",EDGE,{"derivedFrom":subQ0}),-1.0]])]});}
            var Q5;
            Q5=makeQuery(id+"F0.imprint","IMPRINT",FACE,{"disambiguationData":[TD([[makeQuery(id+"F0.imprint","IMPRINT",EDGE,{"derivedFrom":sQuery(id+"F0.wireOp",EDGE,"E13")}),-1.0]])]});
            extrude(context, id + "F2", {"entities" : qUnion([Q0, Q1, Q2, Q3, Q4, Q5]), "depth" : 1.5 * mm, "offsetDistance" : 25 * mm});
        }
        {
            var Q0;
            Q0=makeQuery(id+"F0.imprint","IMPRINT",FACE,{"disambiguationData":[TD([[makeQuery(id+"F0.imprint","IMPRINT",EDGE,{"derivedFrom":sQuery(id+"F0.wireOp",EDGE,"E183.MirrorCS")}),-1.0]])]});
            var Q1;
            Q1=makeQuery(id+"F0.imprint","IMPRINT",FACE,{"disambiguationData":[TD([[makeQuery(id+"F0.imprint","IMPRINT",EDGE,{"derivedFrom":sQuery(id+"F0.wireOp",EDGE,"E0")}),-1.0]])]});
            extrude(context, id + "F3", {"entities" : qUnion([Q0, Q1]), "operationType" : NewBodyOperationType.ADD, "depth" : 2 * mm, "offsetDistance" : 25 * mm});
        }
        {
            var Q0;
            Q0=makeQuery(id+"F0.imprint","IMPRINT",FACE,{"disambiguationData":[TD([[makeQuery(id+"F0.imprint","IMPRINT",EDGE,{"derivedFrom":sQuery(id+"F0.wireOp",EDGE,"E27")}),1.0]])]});
            var Q1;
            Q1=makeQuery(id+"F0.imprint","IMPRINT",FACE,{"disambiguationData":[TD([[makeQuery(id+"F0.imprint","IMPRINT",EDGE,{"derivedFrom":sQuery(id+"F0.wireOp",EDGE,"E160.MirrorCS")}),1.0]])]});
            extrude(context, id + "F4", {"entities" : qUnion([Q0, Q1]), "operationType" : NewBodyOperationType.ADD, "depth" : 2.3 * mm, "offsetDistance" : 25 * mm});
        }
        {
            var Q0;
            {var subQ0=sQuery(id+"F0.wireOp",EDGE,"E50");Q0=makeQuery(id+"F0.imprint","IMPRINT",FACE,{"disambiguationData":[TD([[makeQuery(id+"F0.imprint","IMPRINT",EDGE,{"derivedFrom":subQ0}),1.0]])]});}
            var Q1;
            {var subQ0=sQuery(id+"F0.wireOp",EDGE,"E72");Q1=makeQuery(id+"F0.imprint","IMPRINT",FACE,{"disambiguationData":[TD([[makeQuery(id+"F0.imprint","IMPRINT",EDGE,{"derivedFrom":subQ0}),1.0]])]});}
            var Q2;
            Q2=makeQuery(id+"F0.imprint","IMPRINT",FACE,{"disambiguationData":[TD([[makeQuery(id+"F0.imprint","IMPRINT",EDGE,{"derivedFrom":sQuery(id+"F0.wireOp",EDGE,"E76")}),-1.0]])]});
            var Q3;
            {var subQ2=sQuery(id+"F0.wireOp",EDGE,"E85");Q3=makeQuery(id+"F0.imprint","IMPRINT",FACE,{"disambiguationData":[TD([[makeQuery(id+"F0.imprint","IMPRINT",EDGE,{"derivedFrom":subQ2}),-1.0]])]});}
            var Q4;
            Q4=makeQuery(id+"F0.imprint","IMPRINT",FACE,{"disambiguationData":[TD([[makeQuery(id+"F0.imprint","IMPRINT",EDGE,{"derivedFrom":sQuery(id+"F0.wireOp",EDGE,"E88")}),1.0]])]});
            var Q5;
            {var subQ0=sQuery(id+"F0.wireOp",EDGE,"E92");Q5=makeQuery(id+"F0.imprint","IMPRINT",FACE,{"disambiguationData":[TD([[makeQuery(id+"F0.imprint","IMPRINT",EDGE,{"derivedFrom":subQ0}),1.0]])]});}
            var Q6;
            Q6=makeQuery(id+"F0.imprint","IMPRINT",FACE,{"disambiguationData":[TD([[makeQuery(id+"F0.imprint","IMPRINT",EDGE,{"derivedFrom":sQuery(id+"F0.wireOp",EDGE,"E57")}),1.0]])]});
            var Q7;
            {var subQ1=sQuery(id+"F0.wireOp",EDGE,"E54");Q7=makeQuery(id+"F0.imprint","IMPRINT",FACE,{"disambiguationData":[TD([[makeQuery(id+"F0.imprint","IMPRINT",EDGE,{"derivedFrom":subQ1}),-1.0]])]});}
            var Q8;
            {var subQ0=sQuery(id+"F0.wireOp",EDGE,"E63");Q8=makeQuery(id+"F0.imprint","IMPRINT",FACE,{"disambiguationData":[TD([[makeQuery(id+"F0.imprint","IMPRINT",EDGE,{"derivedFrom":subQ0}),-1.0]])]});}
            var Q9;
            {var subQ5=sQuery(id+"F0.wireOp",EDGE,"E71");Q9=makeQuery(id+"F0.imprint","IMPRINT",FACE,{"disambiguationData":[TD([[makeQuery(id+"F0.imprint","IMPRINT",EDGE,{"derivedFrom":subQ5}),-1.0]])]});}
            var Q10;
            {var subQ0=sQuery(id+"F0.wireOp",EDGE,"E98");Q10=makeQuery(id+"F0.imprint","IMPRINT",FACE,{"disambiguationData":[TD([[makeQuery(id+"F0.imprint","IMPRINT",EDGE,{"derivedFrom":subQ0}),-1.0]])]});}
            var Q11;
            {var subQ0=sQuery(id+"F0.wireOp",EDGE,"E94");Q11=makeQuery(id+"F0.imprint","IMPRINT",FACE,{"disambiguationData":[TD([[makeQuery(id+"F0.imprint","IMPRINT",EDGE,{"derivedFrom":subQ0}),1.0]])]});}
            var Q12;
            {var subQ0=sQuery(id+"F0.wireOp",EDGE,"E64");var subQ1=sQuery(id+"F0.wireOp",EDGE,"E42");var subQ2=makeQuery(id+"F0.imprint","INTERSECT",VERTEX,{"derivedFrom":[subQ1,subQ0]});Q12=makeQuery(id+"F0.imprint","IMPRINT",FACE,{"disambiguationData":[TD([[makeQuery(id+"F0.imprint","IMPRINT",EDGE,{"disambiguationData":[TD([[subQ2,1.0]])],"derivedFrom":subQ1}),1.0]])]});}
            var Q13;
            {var subQ0=sQuery(id+"F0.wireOp",EDGE,"E105");var subQ1=sQuery(id+"F0.wireOp",EDGE,"E101");var subQ2=makeQuery(id+"F0.imprint","INTERSECT",VERTEX,{"derivedFrom":[subQ1,subQ0]});Q13=makeQuery(id+"F0.imprint","IMPRINT",FACE,{"disambiguationData":[TD([[makeQuery(id+"F0.imprint","IMPRINT",EDGE,{"disambiguationData":[TD([[subQ2,-1.0]])],"derivedFrom":subQ1}),-1.0]])]});}
            var Q14;
            {var subQ0=sQuery(id+"F0.wireOp",EDGE,"E103");var subQ1=sQuery(id+"F0.wireOp",EDGE,"E41");var subQ2=makeQuery(id+"F0.imprint","INTERSECT",VERTEX,{"derivedFrom":[subQ1,subQ0]});Q14=makeQuery(id+"F0.imprint","IMPRINT",FACE,{"disambiguationData":[TD([[makeQuery(id+"F0.imprint","IMPRINT",EDGE,{"disambiguationData":[TD([[subQ2,-1.0]])],"derivedFrom":subQ1}),1.0]])]});}
            var Q15;
            {var subQ1=sQuery(id+"F0.wireOp",EDGE,"E42");var subQ3=sQuery(id+"F0.wireOp",EDGE,"E102");var subQ4=makeQuery(id+"F0.imprint","INTERSECT",VERTEX,{"derivedFrom":[subQ1,subQ3]});Q15=makeQuery(id+"F0.imprint","IMPRINT",FACE,{"disambiguationData":[TD([[makeQuery(id+"F0.imprint","IMPRINT",EDGE,{"disambiguationData":[TD([[subQ4,1.0]])],"derivedFrom":subQ3}),-1.0]])]});}
            var Q16;
            {var subQ0=sQuery(id+"F0.wireOp",EDGE,"E73");Q16=makeQuery(id+"F0.imprint","IMPRINT",FACE,{"disambiguationData":[TD([[makeQuery(id+"F0.imprint","IMPRINT",EDGE,{"derivedFrom":subQ0}),1.0]])]});}
            var Q17;
            Q17=makeQuery(id+"F0.imprint","IMPRINT",FACE,{"disambiguationData":[TD([[makeQuery(id+"F0.imprint","IMPRINT",EDGE,{"derivedFrom":sQuery(id+"F0.wireOp",EDGE,"E154.MirrorCS")}),1.0]])]});
            var Q18;
            {var subQ1=sQuery(id+"F0.wireOp",EDGE,"E149.MirrorCS");var subQ3=sQuery(id+"F0.wireOp",EDGE,"E195.MirrorCS");var subQ4=makeQuery(id+"F0.imprint","INTERSECT",VERTEX,{"derivedFrom":[subQ1,subQ3]});Q18=makeQuery(id+"F0.imprint","IMPRINT",FACE,{"disambiguationData":[TD([[makeQuery(id+"F0.imprint","IMPRINT",EDGE,{"disambiguationData":[TD([[subQ4,-1.0]])],"derivedFrom":subQ3}),1.0]])]});}
            var Q19;
            {var subQ0=sQuery(id+"F0.wireOp",EDGE,"E187.MirrorCS");var subQ1=sQuery(id+"F0.wireOp",EDGE,"E185.MirrorCS");var subQ2=makeQuery(id+"F0.imprint","INTERSECT",VERTEX,{"derivedFrom":[subQ1,subQ0]});Q19=makeQuery(id+"F0.imprint","IMPRINT",FACE,{"disambiguationData":[TD([[makeQuery(id+"F0.imprint","IMPRINT",EDGE,{"disambiguationData":[TD([[subQ2,1.0]])],"derivedFrom":subQ1}),-1.0]])]});}
            var Q20;
            {var subQ0=sQuery(id+"F0.wireOp",EDGE,"E186.MirrorCS");var subQ3=sQuery(id+"F0.wireOp",EDGE,"E189.MirrorCS");var subQ5=makeQuery(id+"F0.imprint","INTERSECT",VERTEX,{"derivedFrom":[subQ0,subQ3]});Q20=makeQuery(id+"F0.imprint","IMPRINT",FACE,{"disambiguationData":[TD([[makeQuery(id+"F0.imprint","IMPRINT",EDGE,{"disambiguationData":[TD([[subQ5,1.0]])],"derivedFrom":subQ3}),1.0]])]});}
            var Q21;
            {var subQ0=sQuery(id+"F0.wireOp",EDGE,"E187.MirrorCS");var subQ1=sQuery(id+"F0.wireOp",EDGE,"E149.MirrorCS");var subQ2=makeQuery(id+"F0.imprint","INTERSECT",VERTEX,{"derivedFrom":[subQ1,subQ0]});Q21=makeQuery(id+"F0.imprint","IMPRINT",FACE,{"disambiguationData":[TD([[makeQuery(id+"F0.imprint","IMPRINT",EDGE,{"disambiguationData":[TD([[subQ2,-1.0]])],"derivedFrom":subQ1}),1.0]])]});}
            var Q22;
            {var subQ0=sQuery(id+"F0.wireOp",EDGE,"E186.MirrorCS");var subQ1=sQuery(id+"F0.wireOp",EDGE,"E149.MirrorCS");var subQ2=makeQuery(id+"F0.imprint","INTERSECT",VERTEX,{"derivedFrom":[subQ1,subQ0]});Q22=makeQuery(id+"F0.imprint","IMPRINT",FACE,{"disambiguationData":[TD([[makeQuery(id+"F0.imprint","IMPRINT",EDGE,{"disambiguationData":[TD([[subQ2,1.0]])],"derivedFrom":subQ1}),-1.0]])]});}
            var Q23;
            {var subQ1=sQuery(id+"F0.wireOp",EDGE,"E129.MirrorCS");Q23=makeQuery(id+"F0.imprint","IMPRINT",FACE,{"disambiguationData":[TD([[makeQuery(id+"F0.imprint","IMPRINT",EDGE,{"derivedFrom":subQ1}),1.0]])]});}
            var Q24;
            Q24=makeQuery(id+"F0.imprint","IMPRINT",FACE,{"disambiguationData":[TD([[makeQuery(id+"F0.imprint","IMPRINT",EDGE,{"derivedFrom":sQuery(id+"F0.wireOp",EDGE,"E130.MirrorCS")}),-1.0]])]});
            var Q25;
            Q25=makeQuery(id+"F0.imprint","IMPRINT",FACE,{"disambiguationData":[TD([[makeQuery(id+"F0.imprint","IMPRINT",EDGE,{"derivedFrom":sQuery(id+"F0.wireOp",EDGE,"E133.MirrorCS")}),-1.0]])]});
            var Q26;
            Q26=makeQuery(id+"F0.imprint","IMPRINT",FACE,{"disambiguationData":[TD([[makeQuery(id+"F0.imprint","IMPRINT",EDGE,{"derivedFrom":sQuery(id+"F0.wireOp",EDGE,"E125.MirrorCS")}),1.0]])]});
            var Q27;
            {var subQ6=sQuery(id+"F0.wireOp",EDGE,"E136.MirrorCS");Q27=makeQuery(id+"F0.imprint","IMPRINT",FACE,{"disambiguationData":[TD([[makeQuery(id+"F0.imprint","IMPRINT",EDGE,{"derivedFrom":subQ6}),1.0]])]});}
            var Q28;
            Q28=makeQuery(id+"F0.imprint","IMPRINT",FACE,{"disambiguationData":[TD([[makeQuery(id+"F0.imprint","IMPRINT",EDGE,{"derivedFrom":sQuery(id+"F0.wireOp",EDGE,"E151.MirrorCS")}),-1.0]])]});
            var Q29;
            Q29=makeQuery(id+"F0.imprint","IMPRINT",FACE,{"disambiguationData":[TD([[makeQuery(id+"F0.imprint","IMPRINT",EDGE,{"derivedFrom":sQuery(id+"F0.wireOp",EDGE,"E161.MirrorCS")}),1.0]])]});
            var Q30;
            Q30=makeQuery(id+"F0.imprint","IMPRINT",FACE,{"disambiguationData":[TD([[makeQuery(id+"F0.imprint","IMPRINT",EDGE,{"derivedFrom":sQuery(id+"F0.wireOp",EDGE,"E147.MirrorCS")}),1.0]])]});
            var Q31;
            {var subQ0=sQuery(id+"F0.wireOp",EDGE,"E132.MirrorCS");Q31=makeQuery(id+"F0.imprint","IMPRINT",FACE,{"disambiguationData":[TD([[makeQuery(id+"F0.imprint","IMPRINT",EDGE,{"derivedFrom":subQ0}),1.0]])]});}
            var Q32;
            {var subQ0=sQuery(id+"F0.wireOp",EDGE,"E141.MirrorCS");Q32=makeQuery(id+"F0.imprint","IMPRINT",FACE,{"disambiguationData":[TD([[makeQuery(id+"F0.imprint","IMPRINT",EDGE,{"derivedFrom":subQ0}),-1.0]])]});}
            var Q33;
            {var subQ0=sQuery(id+"F0.wireOp",EDGE,"E75");Q33=makeQuery(id+"F0.imprint","IMPRINT",FACE,{"disambiguationData":[TD([[makeQuery(id+"F0.imprint","IMPRINT",EDGE,{"derivedFrom":subQ0}),-1.0]])]});}
            extrude(context, id + "F5", {"entities" : qUnion([Q0, Q1, Q2, Q3, Q4, Q5, Q6, Q7, Q8, Q9, Q10, Q11, Q12, Q13, Q14, Q15, Q16, Q17, Q18, Q19, Q20, Q21, Q22, Q23, Q24, Q25, Q26, Q27, Q28, Q29, Q30, Q31, Q32, Q33]), "depth" : 1.3 * mm, "offsetDistance" : 25 * mm});
        }
        {
            var Q0;
            {var subQ0=sQuery(id+"F0.wireOp",EDGE,"E185.MirrorCS");var subQ5=sQuery(id+"F0.wireOp",EDGE,"E187.MirrorCS");var subQ6=makeQuery(id+"F0.imprint","INTERSECT",VERTEX,{"derivedFrom":[subQ0,subQ5]});Q0=makeQuery(id+"F0.imprint","IMPRINT",FACE,{"disambiguationData":[TD([[makeQuery(id+"F0.imprint","IMPRINT",EDGE,{"disambiguationData":[TD([[subQ6,1.0]])],"derivedFrom":subQ5}),-1.0]])]});}
            var Q1;
            {var subQ0=sQuery(id+"F0.wireOp",EDGE,"E186.MirrorCS");var subQ1=sQuery(id+"F0.wireOp",EDGE,"E149.MirrorCS");var subQ2=makeQuery(id+"F0.imprint","INTERSECT",VERTEX,{"derivedFrom":[subQ1,subQ0]});Q1=makeQuery(id+"F0.imprint","IMPRINT",FACE,{"disambiguationData":[TD([[makeQuery(id+"F0.imprint","IMPRINT",EDGE,{"disambiguationData":[TD([[subQ2,1.0]])],"derivedFrom":subQ1}),1.0]])]});}
            var Q2;
            {var subQ1=sQuery(id+"F0.wireOp",EDGE,"E130.MirrorCS");Q2=makeQuery(id+"F0.imprint","IMPRINT",FACE,{"disambiguationData":[TD([[makeQuery(id+"F0.imprint","IMPRINT",EDGE,{"derivedFrom":subQ1}),1.0]])]});}
            var Q3;
            {var subQ5=sQuery(id+"F0.wireOp",EDGE,"E129.MirrorCS");Q3=makeQuery(id+"F0.imprint","IMPRINT",FACE,{"disambiguationData":[TD([[makeQuery(id+"F0.imprint","IMPRINT",EDGE,{"derivedFrom":subQ5}),-1.0]])]});}
            var Q4;
            Q4=makeQuery(id+"F0.imprint","IMPRINT",FACE,{"disambiguationData":[TD([[makeQuery(id+"F0.imprint","IMPRINT",EDGE,{"derivedFrom":sQuery(id+"F0.wireOp",EDGE,"E125.MirrorCS")}),-1.0]])]});
            var Q5;
            {var subQ1=sQuery(id+"F0.wireOp",EDGE,"E141.MirrorCS");Q5=makeQuery(id+"F0.imprint","IMPRINT",FACE,{"disambiguationData":[TD([[makeQuery(id+"F0.imprint","IMPRINT",EDGE,{"derivedFrom":subQ1}),1.0]])]});}
            var Q6;
            {var subQ0=sQuery(id+"F0.wireOp",EDGE,"E195.MirrorCS");var subQ1=sQuery(id+"F0.wireOp",EDGE,"E149.MirrorCS");var subQ2=makeQuery(id+"F0.imprint","INTERSECT",VERTEX,{"derivedFrom":[subQ1,subQ0]});Q6=makeQuery(id+"F0.imprint","IMPRINT",FACE,{"disambiguationData":[TD([[makeQuery(id+"F0.imprint","IMPRINT",EDGE,{"disambiguationData":[TD([[subQ2,-1.0]])],"derivedFrom":subQ1}),1.0]])]});}
            var Q7;
            {var subQ0=sQuery(id+"F0.wireOp",EDGE,"E153.MirrorCS");var subQ1=makeQuery(id+"F0.imprint","INTERSECT",VERTEX,{"derivedFrom":[sQuery(id+"F0.wireOp",EDGE,"E140.MirrorCS"),subQ0]});Q7=makeQuery(id+"F0.imprint","IMPRINT",FACE,{"disambiguationData":[TD([[makeQuery(id+"F0.imprint","IMPRINT",EDGE,{"disambiguationData":[TD([[subQ1,1.0]])],"derivedFrom":subQ0}),-1.0]])]});}
            var Q8;
            {var subQ1=sQuery(id+"F0.wireOp",EDGE,"E132.MirrorCS");Q8=makeQuery(id+"F0.imprint","IMPRINT",FACE,{"disambiguationData":[TD([[makeQuery(id+"F0.imprint","IMPRINT",EDGE,{"derivedFrom":subQ1}),-1.0]])]});}
            var Q9;
            Q9=makeQuery(id+"F0.imprint","IMPRINT",FACE,{"disambiguationData":[TD([[makeQuery(id+"F0.imprint","IMPRINT",EDGE,{"derivedFrom":sQuery(id+"F0.wireOp",EDGE,"E147.MirrorCS")}),-1.0]])]});
            var Q10;
            {var subQ0=sQuery(id+"F0.wireOp",EDGE,"E177.MirrorCS");Q10=makeQuery(id+"F0.imprint","IMPRINT",FACE,{"disambiguationData":[TD([[makeQuery(id+"F0.imprint","IMPRINT",EDGE,{"derivedFrom":subQ0}),-1.0]])]});}
            var Q11;
            {var subQ0=sQuery(id+"F0.wireOp",EDGE,"E148.MirrorCS");Q11=makeQuery(id+"F0.imprint","IMPRINT",FACE,{"disambiguationData":[TD([[makeQuery(id+"F0.imprint","IMPRINT",EDGE,{"derivedFrom":subQ0}),-1.0]])]});}
            var Q12;
            {var subQ0=sQuery(id+"F0.wireOp",EDGE,"E136.MirrorCS");Q12=makeQuery(id+"F0.imprint","IMPRINT",FACE,{"disambiguationData":[TD([[makeQuery(id+"F0.imprint","IMPRINT",EDGE,{"derivedFrom":subQ0}),-1.0]])]});}
            var Q13;
            Q13=makeQuery(id+"F0.imprint","IMPRINT",FACE,{"disambiguationData":[TD([[makeQuery(id+"F0.imprint","IMPRINT",EDGE,{"derivedFrom":sQuery(id+"F0.wireOp",EDGE,"E170.MirrorCS")}),-1.0]])]});
            var Q14;
            {var subQ0=sQuery(id+"F0.wireOp",EDGE,"E157.MirrorCS");Q14=makeQuery(id+"F0.imprint","IMPRINT",FACE,{"disambiguationData":[TD([[makeQuery(id+"F0.imprint","IMPRINT",EDGE,{"derivedFrom":subQ0}),1.0]])]});}
            var Q15;
            {var subQ0=sQuery(id+"F0.wireOp",EDGE,"E169.MirrorCS");Q15=makeQuery(id+"F0.imprint","IMPRINT",FACE,{"disambiguationData":[TD([[makeQuery(id+"F0.imprint","IMPRINT",EDGE,{"derivedFrom":subQ0}),1.0]])]});}
            var Q16;
            {var subQ6=sQuery(id+"F0.wireOp",EDGE,"E145.MirrorCS");Q16=makeQuery(id+"F0.imprint","IMPRINT",FACE,{"disambiguationData":[TD([[makeQuery(id+"F0.imprint","IMPRINT",EDGE,{"derivedFrom":subQ6}),-1.0]])]});}
            var Q17;
            {var subQ0=sQuery(id+"F0.wireOp",EDGE,"E143.MirrorCS");Q17=makeQuery(id+"F0.imprint","IMPRINT",FACE,{"disambiguationData":[TD([[makeQuery(id+"F0.imprint","IMPRINT",EDGE,{"derivedFrom":subQ0}),-1.0]])]});}
            var Q18;
            {var subQ0=sQuery(id+"F0.wireOp",EDGE,"E127.MirrorCS");Q18=makeQuery(id+"F0.imprint","IMPRINT",FACE,{"disambiguationData":[TD([[makeQuery(id+"F0.imprint","IMPRINT",EDGE,{"derivedFrom":subQ0}),-1.0]])]});}
            var Q19;
            {var subQ0=sQuery(id+"F0.wireOp",EDGE,"E164.MirrorCS");Q19=makeQuery(id+"F0.imprint","IMPRINT",FACE,{"disambiguationData":[TD([[makeQuery(id+"F0.imprint","IMPRINT",EDGE,{"derivedFrom":subQ0}),1.0]])]});}
            var Q20;
            {var subQ0=sQuery(id+"F0.wireOp",EDGE,"E75");Q20=makeQuery(id+"F0.imprint","IMPRINT",FACE,{"disambiguationData":[TD([[makeQuery(id+"F0.imprint","IMPRINT",EDGE,{"derivedFrom":subQ0}),-1.0]])]});}
            var Q21;
            {var subQ0=sQuery(id+"F0.wireOp",EDGE,"E82");Q21=makeQuery(id+"F0.imprint","IMPRINT",FACE,{"disambiguationData":[TD([[makeQuery(id+"F0.imprint","IMPRINT",EDGE,{"derivedFrom":subQ0}),1.0]])]});}
            var Q22;
            Q22=makeQuery(id+"F0.imprint","IMPRINT",FACE,{"disambiguationData":[TD([[makeQuery(id+"F0.imprint","IMPRINT",EDGE,{"derivedFrom":sQuery(id+"F0.wireOp",EDGE,"E90")}),-1.0]])]});
            var Q23;
            {var subQ0=sQuery(id+"F0.wireOp",EDGE,"E97");Q23=makeQuery(id+"F0.imprint","IMPRINT",FACE,{"disambiguationData":[TD([[makeQuery(id+"F0.imprint","IMPRINT",EDGE,{"derivedFrom":subQ0}),-1.0]])]});}
            var Q24;
            {var subQ3=sQuery(id+"F0.wireOp",EDGE,"E105");var subQ5=sQuery(id+"F0.wireOp",EDGE,"E102");var subQ6=makeQuery(id+"F0.imprint","INTERSECT",VERTEX,{"derivedFrom":[subQ5,subQ3]});Q24=makeQuery(id+"F0.imprint","IMPRINT",FACE,{"disambiguationData":[TD([[makeQuery(id+"F0.imprint","IMPRINT",EDGE,{"disambiguationData":[TD([[subQ6,-1.0]])],"derivedFrom":subQ5}),-1.0]])]});}
            var Q25;
            {var subQ0=sQuery(id+"F0.wireOp",EDGE,"E103");var subQ1=sQuery(id+"F0.wireOp",EDGE,"E101");var subQ2=makeQuery(id+"F0.imprint","INTERSECT",VERTEX,{"derivedFrom":[subQ1,subQ0]});Q25=makeQuery(id+"F0.imprint","IMPRINT",FACE,{"disambiguationData":[TD([[makeQuery(id+"F0.imprint","IMPRINT",EDGE,{"disambiguationData":[TD([[subQ2,-1.0]])],"derivedFrom":subQ1}),-1.0]])]});}
            var Q26;
            {var subQ1=sQuery(id+"F0.wireOp",EDGE,"E99");Q26=makeQuery(id+"F0.imprint","IMPRINT",FACE,{"disambiguationData":[TD([[makeQuery(id+"F0.imprint","IMPRINT",EDGE,{"derivedFrom":subQ1}),1.0]])]});}
            var Q27;
            {var subQ1=sQuery(id+"F0.wireOp",EDGE,"E68");Q27=makeQuery(id+"F0.imprint","IMPRINT",FACE,{"disambiguationData":[TD([[makeQuery(id+"F0.imprint","IMPRINT",EDGE,{"derivedFrom":subQ1}),1.0]])]});}
            var Q28;
            Q28=makeQuery(id+"F0.imprint","IMPRINT",FACE,{"disambiguationData":[TD([[makeQuery(id+"F0.imprint","IMPRINT",EDGE,{"derivedFrom":sQuery(id+"F0.wireOp",EDGE,"E74")}),1.0]])]});
            var Q29;
            {var subQ0=sQuery(id+"F0.wireOp",EDGE,"E50");Q29=makeQuery(id+"F0.imprint","IMPRINT",FACE,{"disambiguationData":[TD([[makeQuery(id+"F0.imprint","IMPRINT",EDGE,{"derivedFrom":subQ0}),-1.0]])]});}
            var Q30;
            {var subQ1=sQuery(id+"F0.wireOp",EDGE,"E51");Q30=makeQuery(id+"F0.imprint","IMPRINT",FACE,{"disambiguationData":[TD([[makeQuery(id+"F0.imprint","IMPRINT",EDGE,{"derivedFrom":subQ1}),-1.0]])]});}
            var Q31;
            {var subQ5=sQuery(id+"F0.wireOp",EDGE,"E60");Q31=makeQuery(id+"F0.imprint","IMPRINT",FACE,{"disambiguationData":[TD([[makeQuery(id+"F0.imprint","IMPRINT",EDGE,{"derivedFrom":subQ5}),1.0]])]});}
            var Q32;
            {var subQ0=sQuery(id+"F0.wireOp",EDGE,"E65");Q32=makeQuery(id+"F0.imprint","IMPRINT",FACE,{"disambiguationData":[TD([[makeQuery(id+"F0.imprint","IMPRINT",EDGE,{"derivedFrom":subQ0}),1.0]])]});}
            var Q33;
            {var subQ0=sQuery(id+"F0.wireOp",EDGE,"E101");var subQ1=sQuery(id+"F0.wireOp",EDGE,"E42");var subQ2=makeQuery(id+"F0.imprint","INTERSECT",VERTEX,{"derivedFrom":[subQ1,subQ0]});Q33=makeQuery(id+"F0.imprint","IMPRINT",FACE,{"disambiguationData":[TD([[makeQuery(id+"F0.imprint","IMPRINT",EDGE,{"disambiguationData":[TD([[subQ2,1.0]])],"derivedFrom":subQ1}),1.0]])]});}
            var Q34;
            {var subQ3=sQuery(id+"F0.wireOp",EDGE,"E63");Q34=makeQuery(id+"F0.imprint","IMPRINT",FACE,{"disambiguationData":[TD([[makeQuery(id+"F0.imprint","IMPRINT",EDGE,{"derivedFrom":subQ3}),1.0]])]});}
            var Q35;
            {var subQ0=sQuery(id+"F0.wireOp",EDGE,"E59");Q35=makeQuery(id+"F0.imprint","IMPRINT",FACE,{"disambiguationData":[TD([[makeQuery(id+"F0.imprint","IMPRINT",EDGE,{"derivedFrom":subQ0}),1.0]])]});}
            var Q36;
            {var subQ0=sQuery(id+"F0.wireOp",EDGE,"E53");Q36=makeQuery(id+"F0.imprint","IMPRINT",FACE,{"disambiguationData":[TD([[makeQuery(id+"F0.imprint","IMPRINT",EDGE,{"derivedFrom":subQ0}),1.0]])]});}
            var Q37;
            {var subQ2=sQuery(id+"F0.wireOp",EDGE,"E89");Q37=makeQuery(id+"F0.imprint","IMPRINT",FACE,{"disambiguationData":[TD([[makeQuery(id+"F0.imprint","IMPRINT",EDGE,{"derivedFrom":subQ2}),-1.0]])]});}
            var Q38;
            {var subQ0=sQuery(id+"F0.wireOp",EDGE,"E87");Q38=makeQuery(id+"F0.imprint","IMPRINT",FACE,{"disambiguationData":[TD([[makeQuery(id+"F0.imprint","IMPRINT",EDGE,{"derivedFrom":subQ0}),1.0]])]});}
            var Q39;
            Q39=makeQuery(id+"F0.imprint","IMPRINT",FACE,{"disambiguationData":[TD([[makeQuery(id+"F0.imprint","IMPRINT",EDGE,{"derivedFrom":sQuery(id+"F0.wireOp",EDGE,"E83")}),1.0]])]});
            extrude(context, id + "F6", {"entities" : qUnion([Q0, Q1, Q2, Q3, Q4, Q5, Q6, Q7, Q8, Q9, Q10, Q11, Q12, Q13, Q14, Q15, Q16, Q17, Q18, Q19, Q20, Q21, Q22, Q23, Q24, Q25, Q26, Q27, Q28, Q29, Q30, Q31, Q32, Q33, Q34, Q35, Q36, Q37, Q38, Q39]), "depth" : 1 * mm, "offsetDistance" : 25 * mm});
        }
        {
            var Q0;
            {var subQ7=sQuery(id+"F0.wireOp",EDGE,"E188.MirrorCS");Q0=makeQuery(id+"F0.imprint","IMPRINT",FACE,{"disambiguationData":[TD([[makeQuery(id+"F0.imprint","IMPRINT",EDGE,{"derivedFrom":subQ7}),1.0]])]});}
            var Q1;
            Q1=makeQuery(id+"F0.imprint","IMPRINT",FACE,{"disambiguationData":[TD([[makeQuery(id+"F0.imprint","IMPRINT",EDGE,{"derivedFrom":sQuery(id+"F0.wireOp",EDGE,"E21")}),1.0]])]});
            var Q2;
            {var subQ0=sQuery(id+"F0.wireOp",EDGE,"E251");var subQ1=sQuery(id+"F0.wireOp",EDGE,"E24");var subQ2=makeQuery(id+"F0.imprint","INTERSECT",VERTEX,{"derivedFrom":[subQ1,subQ0]});Q2=makeQuery(id+"F0.imprint","IMPRINT",FACE,{"disambiguationData":[TD([[makeQuery(id+"F0.imprint","IMPRINT",EDGE,{"disambiguationData":[TD([[subQ2,-1.0]])],"derivedFrom":subQ1}),1.0]])]});}
            var Q3;
            {var subQ3=sQuery(id+"F0.wireOp",EDGE,"E231.MirrorCS");var subQ7=sQuery(id+"F0.wireOp",EDGE,"E251");var subQ8=makeQuery(id+"F0.imprint","INTERSECT",VERTEX,{"derivedFrom":[subQ3,subQ7]});Q3=makeQuery(id+"F0.imprint","IMPRINT",FACE,{"disambiguationData":[TD([[makeQuery(id+"F0.imprint","IMPRINT",EDGE,{"disambiguationData":[TD([[subQ8,-1.0]])],"derivedFrom":subQ3}),1.0]])]});}
            var Q4;
            {var subQ3=sQuery(id+"F0.wireOp",EDGE,"E251");var subQ7=sQuery(id+"F0.wireOp",EDGE,"E24");var subQ9=makeQuery(id+"F0.imprint","INTERSECT",VERTEX,{"derivedFrom":[subQ7,subQ3]});Q4=makeQuery(id+"F0.imprint","IMPRINT",FACE,{"disambiguationData":[TD([[makeQuery(id+"F0.imprint","IMPRINT",EDGE,{"disambiguationData":[TD([[subQ9,-1.0]])],"derivedFrom":subQ7}),-1.0]])]});}
            var Q5;
            {var subQ6=sQuery(id+"F0.wireOp",EDGE,"E257");Q5=makeQuery(id+"F0.imprint","IMPRINT",FACE,{"disambiguationData":[TD([[makeQuery(id+"F0.imprint","IMPRINT",EDGE,{"derivedFrom":subQ6}),1.0]])]});}
            extrude(context, id + "F7", {"entities" : qUnion([Q0, Q1, Q2, Q3, Q4, Q5]), "operationType" : NewBodyOperationType.ADD, "depth" : 2 * mm, "offsetDistance" : 25 * mm});
        }
        {
            var Q0;
            {var subQ1=sQuery(id+"F0.wireOp",EDGE,"E188.MirrorCS");Q0=makeQuery(id+"F0.imprint","IMPRINT",FACE,{"disambiguationData":[TD([[makeQuery(id+"F0.imprint","IMPRINT",EDGE,{"derivedFrom":subQ1}),-1.0]])]});}
            var Q1;
            {var subQ6=sQuery(id+"F0.wireOp",EDGE,"E113");Q1=makeQuery(id+"F0.imprint","IMPRINT",FACE,{"disambiguationData":[TD([[makeQuery(id+"F0.imprint","IMPRINT",EDGE,{"derivedFrom":subQ6}),1.0]])]});}
            var Q2;
            {var subQ0=sQuery(id+"F0.wireOp",EDGE,"E204.MirrorCS");Q2=makeQuery(id+"F0.imprint","IMPRINT",FACE,{"disambiguationData":[TD([[makeQuery(id+"F0.imprint","IMPRINT",EDGE,{"derivedFrom":subQ0}),-1.0]])]});}
            var Q3;
            {var subQ0=sQuery(id+"F0.wireOp",EDGE,"E114");Q3=makeQuery(id+"F0.imprint","IMPRINT",FACE,{"disambiguationData":[TD([[makeQuery(id+"F0.imprint","IMPRINT",EDGE,{"derivedFrom":subQ0}),1.0]])]});}
            var Q4;
            {var subQ0=sQuery(id+"F0.wireOp",EDGE,"E200.MirrorCS");Q4=makeQuery(id+"F0.imprint","IMPRINT",FACE,{"disambiguationData":[TD([[makeQuery(id+"F0.imprint","IMPRINT",EDGE,{"derivedFrom":subQ0}),-1.0]])]});}
            var Q5;
            {var subQ0=sQuery(id+"F0.wireOp",EDGE,"E123");Q5=makeQuery(id+"F0.imprint","IMPRINT",FACE,{"disambiguationData":[TD([[makeQuery(id+"F0.imprint","IMPRINT",EDGE,{"derivedFrom":subQ0}),1.0]])]});}
            var Q6;
            {var subQ2=sQuery(id+"F0.wireOp",EDGE,"E198.MirrorCS");Q6=makeQuery(id+"F0.imprint","IMPRINT",FACE,{"disambiguationData":[TD([[makeQuery(id+"F0.imprint","IMPRINT",EDGE,{"derivedFrom":subQ2}),-1.0]])]});}
            var Q7;
            {var subQ0=sQuery(id+"F0.wireOp",EDGE,"E121");Q7=makeQuery(id+"F0.imprint","IMPRINT",FACE,{"disambiguationData":[TD([[makeQuery(id+"F0.imprint","IMPRINT",EDGE,{"derivedFrom":subQ0}),1.0]])]});}
            var Q8;
            {var subQ0=sQuery(id+"F0.wireOp",EDGE,"E106");Q8=makeQuery(id+"F0.imprint","IMPRINT",FACE,{"disambiguationData":[TD([[makeQuery(id+"F0.imprint","IMPRINT",EDGE,{"derivedFrom":subQ0}),1.0]])]});}
            var Q9;
            {var subQ0=sQuery(id+"F0.wireOp",EDGE,"E201.MirrorCS");Q9=makeQuery(id+"F0.imprint","IMPRINT",FACE,{"disambiguationData":[TD([[makeQuery(id+"F0.imprint","IMPRINT",EDGE,{"derivedFrom":subQ0}),-1.0]])]});}
            var Q10;
            Q10=makeQuery(id+"F0.imprint","IMPRINT",FACE,{"disambiguationData":[TD([[makeQuery(id+"F0.imprint","IMPRINT",EDGE,{"derivedFrom":sQuery(id+"F0.wireOp",EDGE,"E199.MirrorCS")}),-1.0]])]});
            var Q11;
            Q11=makeQuery(id+"F0.imprint","IMPRINT",FACE,{"disambiguationData":[TD([[makeQuery(id+"F0.imprint","IMPRINT",EDGE,{"derivedFrom":sQuery(id+"F0.wireOp",EDGE,"E117")}),1.0]])]});
            var Q12;
            {var subQ0=sQuery(id+"F0.wireOp",EDGE,"E197.MirrorCS");Q12=makeQuery(id+"F0.imprint","IMPRINT",FACE,{"disambiguationData":[TD([[makeQuery(id+"F0.imprint","IMPRINT",EDGE,{"derivedFrom":subQ0}),-1.0]])]});}
            var Q13;
            {var subQ0=sQuery(id+"F0.wireOp",EDGE,"E119");Q13=makeQuery(id+"F0.imprint","IMPRINT",FACE,{"disambiguationData":[TD([[makeQuery(id+"F0.imprint","IMPRINT",EDGE,{"derivedFrom":subQ0}),1.0]])]});}
            var Q14;
            {var subQ2=sQuery(id+"F0.wireOp",EDGE,"E207.MirrorCS");Q14=makeQuery(id+"F0.imprint","IMPRINT",FACE,{"disambiguationData":[TD([[makeQuery(id+"F0.imprint","IMPRINT",EDGE,{"derivedFrom":subQ2}),-1.0]])]});}
            var Q15;
            {var subQ0=sQuery(id+"F0.wireOp",EDGE,"E108");Q15=makeQuery(id+"F0.imprint","IMPRINT",FACE,{"disambiguationData":[TD([[makeQuery(id+"F0.imprint","IMPRINT",EDGE,{"derivedFrom":subQ0}),1.0]])]});}
            var Q16;
            {var subQ0=sQuery(id+"F0.wireOp",EDGE,"E202.MirrorCS");Q16=makeQuery(id+"F0.imprint","IMPRINT",FACE,{"disambiguationData":[TD([[makeQuery(id+"F0.imprint","IMPRINT",EDGE,{"derivedFrom":subQ0}),-1.0]])]});}
            var Q17;
            {var subQ0=sQuery(id+"F0.wireOp",EDGE,"E110");Q17=makeQuery(id+"F0.imprint","IMPRINT",FACE,{"disambiguationData":[TD([[makeQuery(id+"F0.imprint","IMPRINT",EDGE,{"derivedFrom":subQ0}),1.0]])]});}
            var Q18;
            {var subQ1=sQuery(id+"F0.wireOp",EDGE,"E7");var subQ3=sQuery(id+"F0.wireOp",EDGE,"E251");var subQ4=makeQuery(id+"F0.imprint","INTERSECT",VERTEX,{"derivedFrom":[subQ1,subQ3]});Q18=makeQuery(id+"F0.imprint","IMPRINT",FACE,{"disambiguationData":[TD([[makeQuery(id+"F0.imprint","IMPRINT",EDGE,{"disambiguationData":[TD([[subQ4,1.0]])],"derivedFrom":subQ3}),1.0]])]});}
            var Q19;
            {var subQ1=sQuery(id+"F0.wireOp",EDGE,"E7");var subQ3=sQuery(id+"F0.wireOp",EDGE,"E251");var subQ4=makeQuery(id+"F0.imprint","INTERSECT",VERTEX,{"derivedFrom":[subQ1,subQ3]});Q19=makeQuery(id+"F0.imprint","IMPRINT",FACE,{"disambiguationData":[TD([[makeQuery(id+"F0.imprint","IMPRINT",EDGE,{"disambiguationData":[TD([[subQ4,-1.0]])],"derivedFrom":subQ3}),1.0]])]});}
            extrude(context, id + "F8", {"entities" : qUnion([Q0, Q1, Q2, Q3, Q4, Q5, Q6, Q7, Q8, Q9, Q10, Q11, Q12, Q13, Q14, Q15, Q16, Q17, Q18, Q19]), "operationType" : NewBodyOperationType.ADD, "depth" : 2.8 * mm, "offsetDistance" : 25 * mm});
        }
    });
